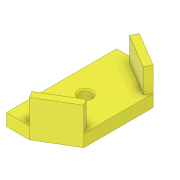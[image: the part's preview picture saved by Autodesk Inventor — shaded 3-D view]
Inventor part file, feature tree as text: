
AUTODESK INVENTOR PART (.ipt)
format: ipt  version: 2019.4 (Build 234330000, 330)  size: 180,224 bytes
history: native  units: mm
features: extrude x5, sketch x5, projected_geometry x4, chamfer x1
ambient origin geometry x8: Origin, YZ Plane, XZ Plane, XY Plane, X Axis, Y Axis, Z Axis, Center Point
bodies: Solid1 (feature_tree)
feature tree (15):
  extrude  "Extrusion1"  Depth=30.0mm TaperAngle=360.0deg
  extrude  "Extrusion2"  Depth=6.0mm
  extrude  "Extrusion3"  Depth=15.0mm
  extrude  "Extrusion5"  Depth=4.0mm TaperAngle=0.0deg
  extrude  "Extrusion6"  Depth=1.0mm TaperAngle=0.0deg
  chamfer  "Chamfer1"  Distance=9.0mm
  sketch  "Sketch1"  dims[d2=8.0mm d4=30.0mm d6=360.0deg]
  sketch  "Sketch2"  dims[d8=6.0mm d9=6.0mm]
  projected_geometry  "Projected Loop1"
  sketch  "Sketch3"  dims[d11=15.0mm d1=12.0mm]
  projected_geometry  "Projected Loop2"
  sketch  "Sketch5"  dims[d13=12.0mm d14=4.0mm d15=0.0mm]
  projected_geometry  "Projected Loop3"
  sketch  "Sketch6"  dims[d16=5.0mm d17=1.0mm d18=0.0mm d19=9.0mm d20=9.0mm d21=15.0mm d22=15.0mm d23=0.5mm d24=0.0mm d27=4.0mm d28=0.5mm d29=0.0mm d30=3.0mm d31=3.0mm d32=10.0mm d33=0.0mm d35=5.0mm d36=0.5mm d37=2.0mm d38=45.0deg]
  projected_geometry  "Projected Loop4"
